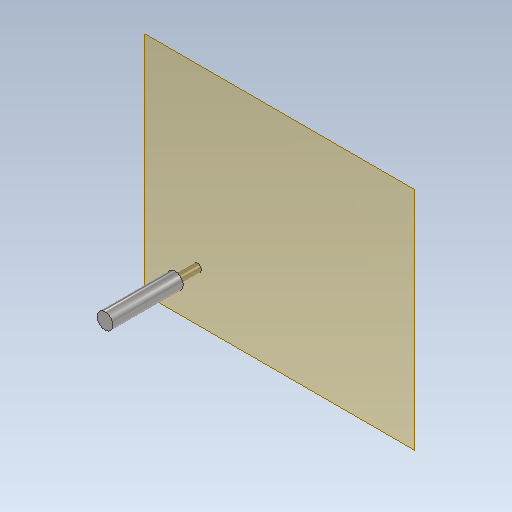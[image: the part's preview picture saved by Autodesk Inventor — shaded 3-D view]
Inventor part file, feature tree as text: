
AUTODESK INVENTOR PART (.ipt)
format: ipt  version: 2020 (Build 240168000, 168)  size: 104,960 bytes
history: native  units: in
note: dims shown in document units (in); Inventor stores cm internally (conversion verified against a paired STEP export)
features: other x6, plane x2, extrude x2, sketch x2, reference x1
ambient origin geometry x8: Origin, YZ Plane, XZ Plane, XY Plane, X Axis, Y Axis, Z Axis, Center Point
bodies: Solid1 (feature_tree)
feature tree (13):
  plane  "Work Plane1"
  extrude  "Extrusion1"  Depth=0.25in
  plane  "Work Plane2"
  extrude  "Extrusion3"  [1 undecoded]
  sketch  "Sketch1"  dims[d0=0.25in d1=0.0in d5=0.1772in]
  reference  "Reference1"
  sketch  "Sketch2"  dims[d6=0.7874in d7=0.0in]
  other  "<userpath>\Documents\Inventor\Drone\Assembly.iam"
  other  "Assembly.iam"
  other  "Frame:1"
  other  "DJI F330 qoadrotor arm:1"
  other  "DJI F330 qoadrotor arm v2"
  other  "holder:1"
note: 1 required parameter value undecoded (feature->parameter linkage not recoverable at this tier; creation-order binding heuristic only, values carry confidence <= 0.55)
